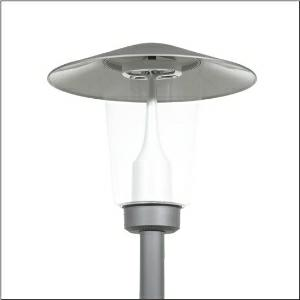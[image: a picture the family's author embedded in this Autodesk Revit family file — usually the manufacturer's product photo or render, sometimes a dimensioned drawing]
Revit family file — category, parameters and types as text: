
# Revit family: pilzleuchte_iq___st1_2a_5xa5235kf14h_dd17
name_source: partatom
category: Lighting Fixtures
units: mm (PartAtom-declared; Revit-internal decimal feet)

## family parameters
Cut with Voids When Loaded = No
Host = Face
Light Source = No
Part Type = Normal
Room Calculation Point = No
Round Connector Dimension = Use Diameter
Shared = No

## types (1)
- --- (1 x LED, 1550 lm, 10 W, 4000K)
    Apparent Load = 10 VA
    CIE Flux Codes = 24 61 93 98 100
    Color Rendering = 70
    Color Temperature = 4000K
    Default Elevation = 1800 mm
    Description = Mushroom Luminaire iQ, mast luminaire, Module 540 iQ-SR, primary light control with 3 zone facetted reflector, of plastic, silver coated, highly specular, structured, primary optical cover: cover, of PMMA, transparent, light distribution: ST1.2a, light emission: direct distribution, primary light characteristic: asymmetric, installation type: post-top, LED, High Power LED, rated luminous flux: 1.550lm, luminous efficacy: 155lm/W, light colour: 740, colour temperature: 4000K, control gear: ECG iQ, control: presetting dimming logarithmic, Street-Remote, Auto-Match, Temp-Guard, Lumen-Switch, Night-Set, Smart-Wire, Light-Fading, Desk-Remote (wireless, voltage-free reading and setting of iQ features in the workshop via application-optimized NFC function/RFID function), optimised constant luminous flux control (CLO 2.0), with terminal, 6-pole, max. 2.5mm², mains connection: 220..240V, AC, 50/60Hz, start of lifetime: 10W, end of lifetime: 10W, reduction: 5W, luminaire housing, upper part, of glass-fibre reinforced polyester, coated, Siteco® metallic grey (DB 702S), diameter: 650mm, height: 586mm, spigot size: d x l = 76 x 70mm (post-top) | with reducer (optional accessory) 60 x 70mm, post-top mast mounting element, of diecast aluminium, coated, Siteco® metallic grey (DB 702S), Module 540 iQ-SR, traffic white (RAL 9016), equipment: standard, protection rating (complete): IP65, insulation class (complete): insulation class II (safety insulation), certification: CE, ENEC, VDE, packaging unit: 1 piece

Light Distribution: ST1.2a
    Height = 586 mm
    Lamp = 1 x LED
    Lamp Light Flux = 1550 lm
    Lamp Power = 10 W
    Lamp count = 1
    Length = 650 mm
    Luminous efficacy = 155 lm/W
    Manufacturer = Siteco
    ModVariant = No
    Model = 5XA5235KF14H
    Number of Poles = 1
    OnlyDefault = Yes
    Power Factor = 1
    Product Name = Pilzleuchte iQ | ST1.2a
    Product group = mast luminaire | pylon top
    ProductGroupID = 6100
    Protection Class = Protection class II
    Protection Degree = IP 65
    RLX_Detail_Level = 1
    RlxData = <blob elided: 127193 chars, md5=861cc3f4>
    Socket = socket
    Standby Power = 0 W
    System Light Flux = 1550 lm
    System Power = 10 W
    Type Comments = factory setting: luminous flux: 100 % | dim-lin: 254 | 401 mA
    Type Image = l_1006077.jpg
    URL = http://relux.com
    VarID = @adj_071979
    Voltage = 0 V
    Weight = 0.00 kg
    Width = 0 mm  [stored 0 ft]

note: [stored X ft] marks values corroborated as IEEE doubles in the binary element streams (Revit-internal decimal feet)

## geometry (parser evidence)
native form markers: Blend x4, Sweep x10
no freeform markers — native parametric forms only
